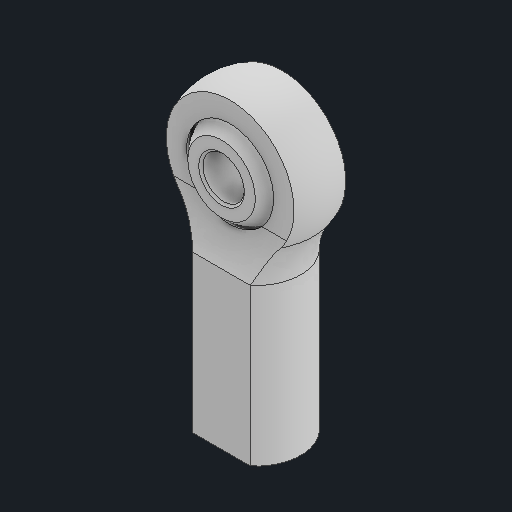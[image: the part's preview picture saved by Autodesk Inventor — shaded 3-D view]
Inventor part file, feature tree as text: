
AUTODESK INVENTOR PART (.ipt)
format: ipt  version: 2023 (Build 270158000, 158)  size: 494,080 bytes
history: native  units: in
note: dims shown in document units (in); Inventor stores cm internally (conversion verified against a paired STEP export)
features: fillet x1, chamfer x1
ambient origin geometry x8: Origin, YZ Plane, XZ Plane, XY Plane, X Axis, Y Axis, Z Axis, Center Point
bodies: Solid1 (feature_tree), Solid2 (feature_tree)
feature tree (2):
  fillet  "Fillet1"  [1 undecoded]
  chamfer  "Chamfer1"  [1 undecoded]
note: 2 required parameter values undecoded (feature->parameter linkage not recoverable at this tier; creation-order binding heuristic only, values carry confidence <= 0.55)
